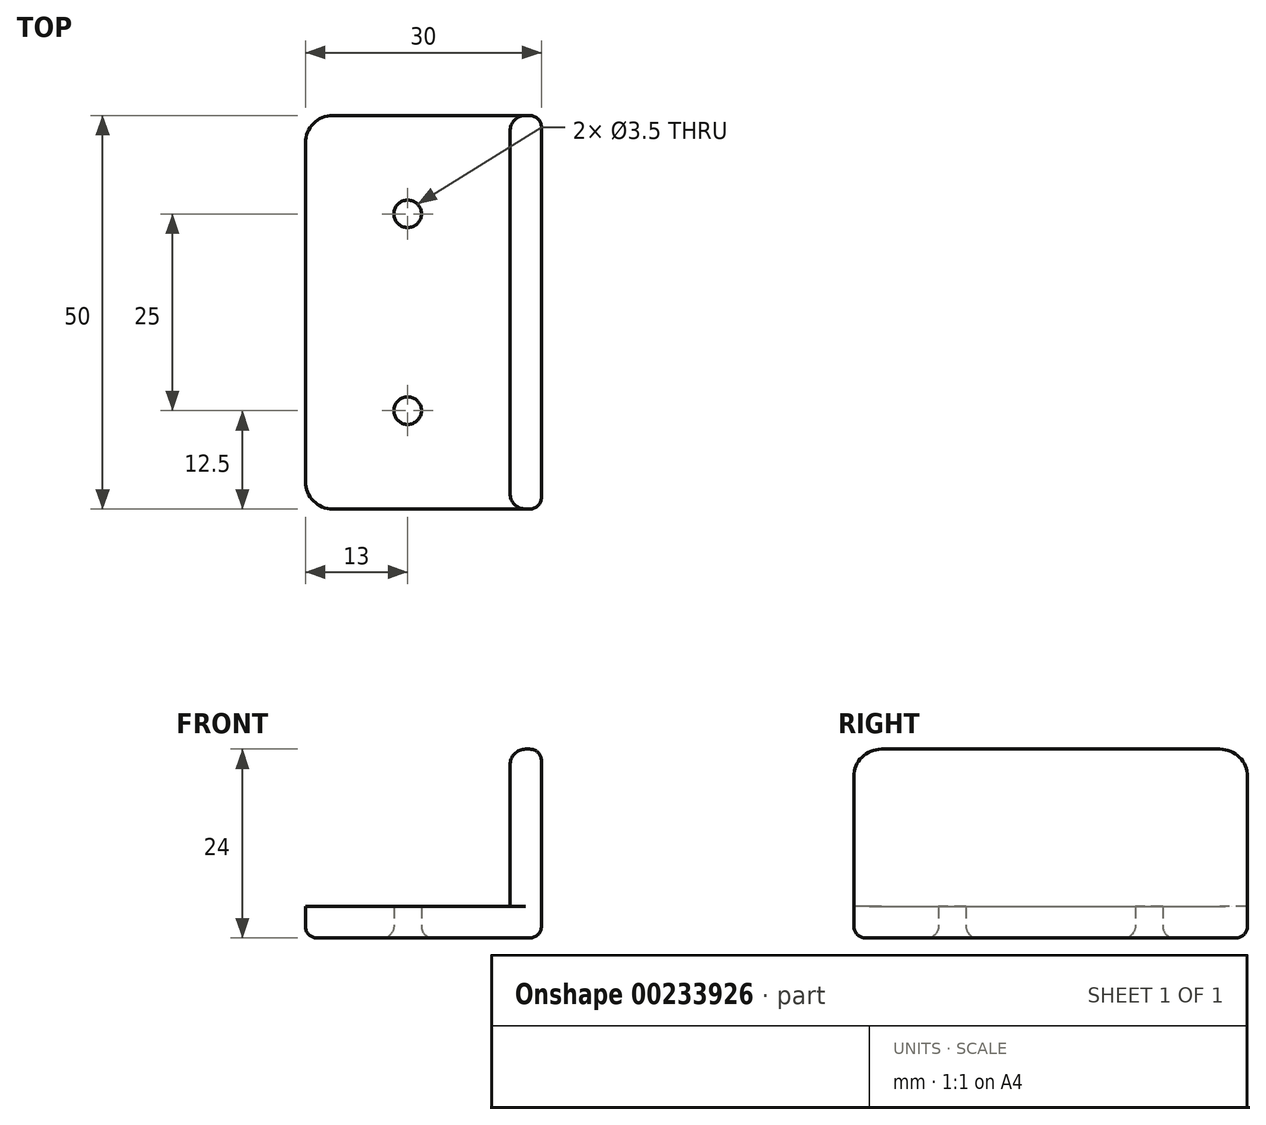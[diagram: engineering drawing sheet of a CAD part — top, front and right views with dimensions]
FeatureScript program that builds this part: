
annotation { "Feature Type Name" : "Feature", "Feature Type Description" : "" }
export const myFeature = defineFeature(function(context is Context, id is Id, definition is map)
    precondition{}
    {
        {
            var Q0;
            Q0=qCreatedBy(makeId("Top.planeOp"),FACE);
            var sketch = newSketch(context, id + "F0", { "sketchPlane" : qUnion([Q0])});
            skLineSegment(sketch, "E0.bottom", {"start": v(0, 0) * mm, "end": v(-26, 0) * mm});
            skLineSegment(sketch, "E0.top", {"start": v(0, 25) * mm, "end": v(-22.5, 25) * mm});
            skLineSegment(sketch, "E0.left", {"start": v(0, 0) * mm, "end": v(0, 25) * mm});
            skLineSegment(sketch, "E0.right", {"start": v(-26, 0) * mm, "end": v(-26, 21.5) * mm});
            skLineSegment(sketch, "E1.MirrorCS", {"start": v(-26, 0) * mm, "end": v(-26, -21.5) * mm});
            skLineSegment(sketch, "E2.MirrorCS", {"start": v(0, -25) * mm, "end": v(-22.5, -25) * mm});
            skLineSegment(sketch, "E3.MirrorCS", {"start": v(0, 0) * mm, "end": v(0, -25) * mm});
            skLineSegment(sketch, "E4", {"start": v(0, 25) * mm, "end": v(4, 25) * mm});
            skLineSegment(sketch, "E5", {"start": v(4, 25) * mm, "end": v(4, -25) * mm});
            skLineSegment(sketch, "E6", {"start": v(4, -25) * mm, "end": v(0, -25) * mm});
            skCircle(sketch, "E7", {"center": v(-13, 12.5) * mm, "radius": 1.75 * mm});
            skPoint(sketch, "E7.centerSnap0", {"position": v(-13, 25) * mm});
            skPoint(sketch, "E7.centerSnap1", {"position": v(-26, 12.5) * mm});
            skCircle(sketch, "E8", {"center": v(-13, -12.5) * mm, "radius": 1.75 * mm});
            skPoint(sketch, "E8.centerSnap0", {"position": v(-13, -25) * mm});
            skPoint(sketch, "E8.centerSnap1", {"position": v(-26, -12.5) * mm});
            skPoint(sketch, "E9.visualSharp", {"position": v(-26, -25) * mm});
            skArc(sketch, "E9.filletArc", {"start": v(-26, -21.5) * mm, "mid": v(-24.97, -23.97) * mm, "end": v(-22.5, -25) * mm});
            skPoint(sketch, "E10.visualSharp", {"position": v(-26, 25) * mm});
            skArc(sketch, "E10.filletArc", {"start": v(-22.5, 25) * mm, "mid": v(-24.97, 23.97) * mm, "end": v(-26, 21.5) * mm});
            skSolve(sketch);
        }
        {
            var Q0;
            Q0=makeQuery(id+"F0.imprint","IMPRINT",FACE,{"disambiguationData":[TD([[makeQuery(id+"F0.imprint","IMPRINT",EDGE,{"derivedFrom":sQuery(id+"F0.wireOp",EDGE,"E0.bottom")}),-1.0]])]});
            var Q1;
            Q1=makeQuery(id+"F0.imprint","IMPRINT",FACE,{"disambiguationData":[TD([[makeQuery(id+"F0.imprint","IMPRINT",EDGE,{"derivedFrom":sQuery(id+"F0.wireOp",EDGE,"E0.bottom")}),1.0]])]});
            extrude(context, id + "F1", {"entities" : qUnion([Q0, Q1]), "depth" : 4 * mm});
        }
        {
            var Q0;
            Q0=makeQuery(id+"F0.imprint","IMPRINT",FACE,{"disambiguationData":[TD([[makeQuery(id+"F0.imprint","IMPRINT",EDGE,{"derivedFrom":sQuery(id+"F0.wireOp",EDGE,"E0.left")}),-1.0]])]});
            extrude(context, id + "F2", {"entities" : qUnion([Q0]), "operationType" : NewBodyOperationType.ADD, "depth" : 24 * mm});
        }
        {
            var Q0;
            Q0=makeQuery(id+"F2.opExtrude","CAP_EDGE",EDGE,{"disambiguationData":[OSD([sQuery(id+"F0.wireOp",EDGE,"E4")])],"isStart":false});
            var Q1;
            Q1=makeQuery(id+"F2.opExtrude","CAP_EDGE",EDGE,{"disambiguationData":[OSD([sQuery(id+"F0.wireOp",EDGE,"E6")])],"isStart":false});
            fillet(context, id + "F3", {"entities" : qUnion([Q0, Q1]), "radius" : 3.5 * mm, "tangentPropagation" : true, "allowEdgeOverflow" : false});
        }
        {
            var Q0;
            {var subQ0=sQuery(id+"F0.wireOp",EDGE,"E3.MirrorCS");var subQ1=sQuery(id+"F0.wireOp",EDGE,"E0.left");Q0=makeQuery(id+"F2.boolean.opBoolean","MERGE",FACE,{"derivedFrom":[makeQuery(id+"F1.opExtrude","CAP_FACE",FACE,{"disambiguationData":[OSD([sQuery(id+"F0.wireOp",EDGE,"E0.top"),subQ1,sQuery(id+"F0.wireOp",EDGE,"E0.right"),sQuery(id+"F0.wireOp",EDGE,"E1.MirrorCS"),sQuery(id+"F0.wireOp",EDGE,"E2.MirrorCS"),subQ0,sQuery(id+"F0.wireOp",EDGE,"E7"),sQuery(id+"F0.wireOp",EDGE,"E8")])],"isStart":true}),makeQuery(id+"F2.opExtrude","CAP_FACE",FACE,{"disambiguationData":[OSD([subQ1,subQ0,sQuery(id+"F0.wireOp",EDGE,"E4"),sQuery(id+"F0.wireOp",EDGE,"E5"),sQuery(id+"F0.wireOp",EDGE,"E6")])],"isStart":true})]});}
            var Q1;
            Q1=makeQuery(id+"F2.opExtrude","SWEPT_FACE",FACE,{"disambiguationData":[OSD([sQuery(id+"F0.wireOp",EDGE,"E5")])]});
            fillet(context, id + "F4", {"entities" : qUnion([Q0, Q1]), "radius" : 1.5 * mm, "tangentPropagation" : true, "allowEdgeOverflow" : false});
        }
        {
            var Q0;
            Q0=makeQuery(id+"F2.opExtrude","CAP_EDGE",EDGE,{"disambiguationData":[OSD([sQuery(id+"F0.wireOp",EDGE,"E0.left"),sQuery(id+"F0.wireOp",EDGE,"E3.MirrorCS")])],"isStart":false});
            var Q1;
            Q1=makeQuery(id+"F2.opExtrude","SWEPT_EDGE",EDGE,{"disambiguationData":[OSD([sQuery(id+"F0.wireOp",EDGE,"E2.MirrorCS"),sQuery(id+"F0.wireOp",EDGE,"E3.MirrorCS"),sQuery(id+"F0.wireOp",EDGE,"E6")])]});
            var Q2;
            Q2=makeQuery(id+"F2.opExtrude","SWEPT_EDGE",EDGE,{"disambiguationData":[OSD([sQuery(id+"F0.wireOp",EDGE,"E0.top"),sQuery(id+"F0.wireOp",EDGE,"E0.left"),sQuery(id+"F0.wireOp",EDGE,"E4")])]});
            fillet(context, id + "F5", {"entities" : qUnion([Q0, Q1, Q2]), "radius" : 2 * mm, "tangentPropagation" : true, "allowEdgeOverflow" : false});
        }
    });
